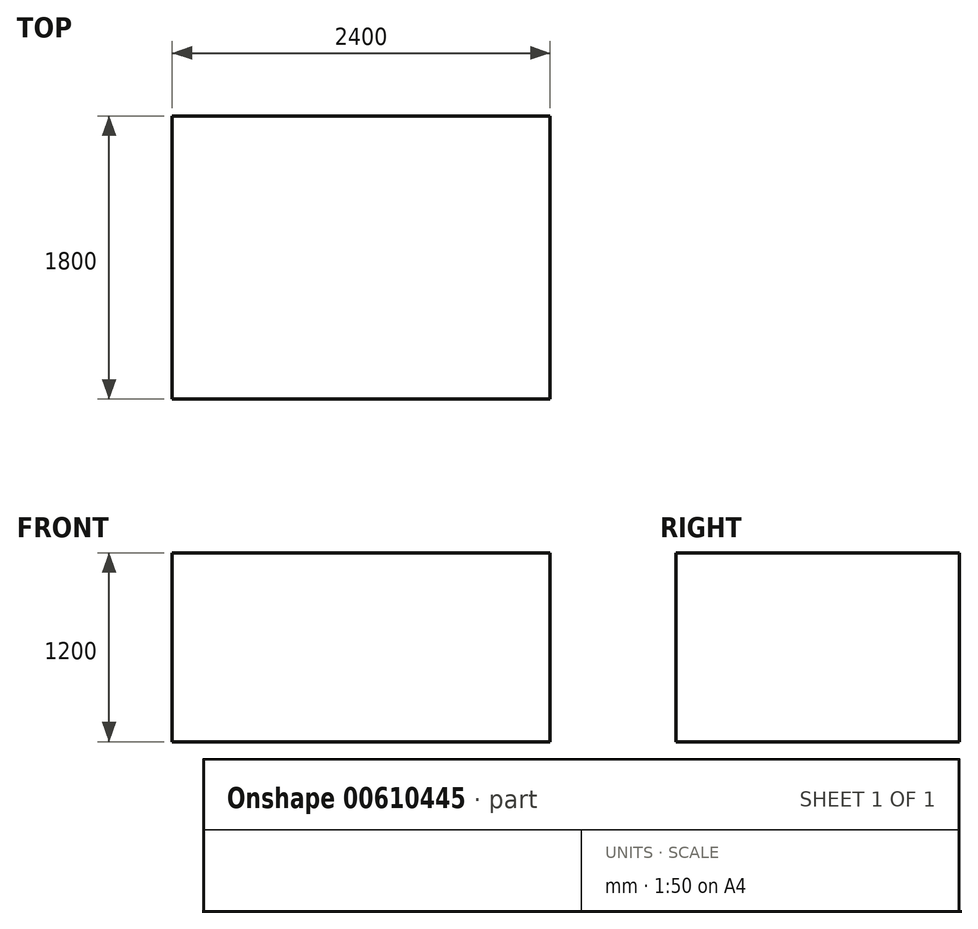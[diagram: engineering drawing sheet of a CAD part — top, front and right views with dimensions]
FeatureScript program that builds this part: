
annotation { "Feature Type Name" : "Feature", "Feature Type Description" : "" }
export const myFeature = defineFeature(function(context is Context, id is Id, definition is map)
    precondition{}
    {
        {
            var Q0;
            Q0=qCreatedBy(makeId("Front.planeOp"),FACE);
            var sketch = newSketch(context, id + "F0", { "sketchPlane" : qUnion([Q0])});
            skLineSegment(sketch, "E0.bottom", {"start": v(0, 0) * mm, "end": v(2400, 0) * mm});
            skLineSegment(sketch, "E0.top", {"start": v(0, 1200) * mm, "end": v(2400, 1200) * mm});
            skLineSegment(sketch, "E0.left", {"start": v(0, 0) * mm, "end": v(0, 1200) * mm});
            skLineSegment(sketch, "E0.right", {"start": v(2400, 0) * mm, "end": v(2400, 1200) * mm});
            skSolve(sketch);
        }
        {
            var Q0;
            Q0 = qSketchRegion(id + "F0", true);
            extrude(context, id + "F1", {"entities" : qUnion([Q0]), "depth" : 1800 * mm, "offsetDistance" : 25.4 * mm});
        }
    });
